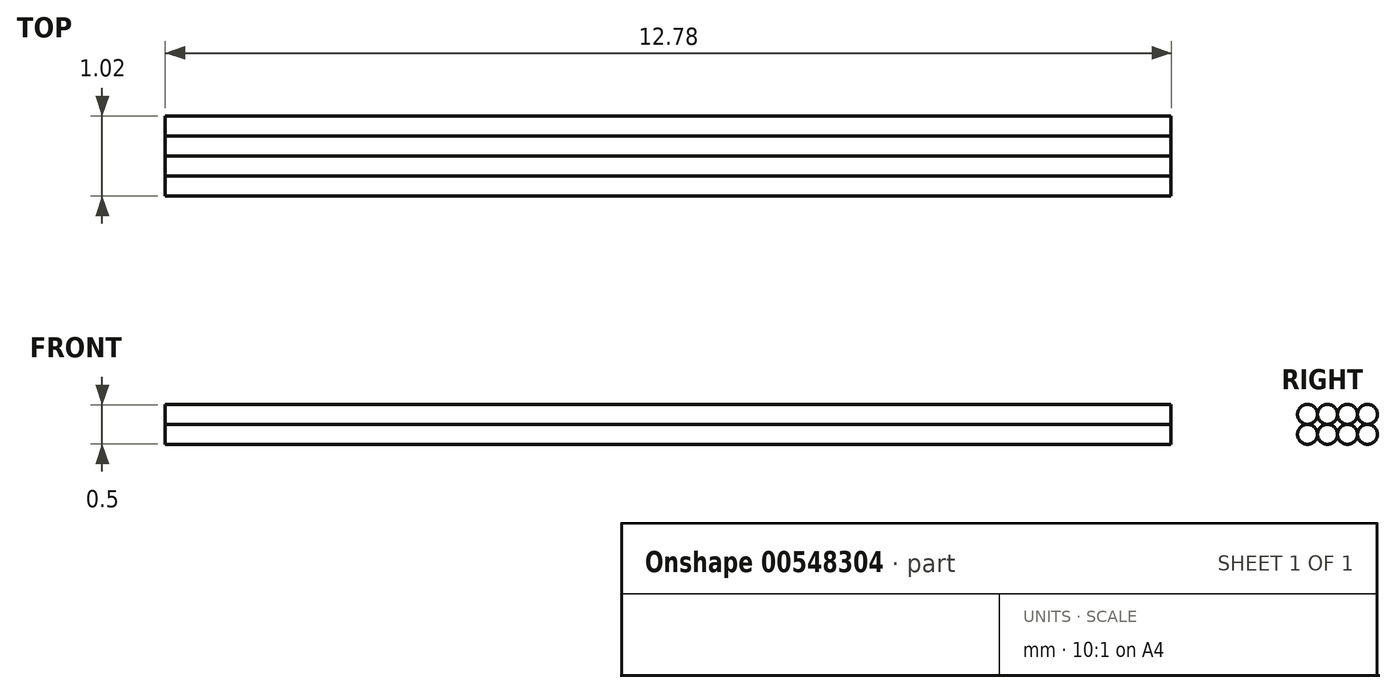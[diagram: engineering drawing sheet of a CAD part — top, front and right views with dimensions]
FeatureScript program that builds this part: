
annotation { "Feature Type Name" : "Feature", "Feature Type Description" : "" }
export const myFeature = defineFeature(function(context is Context, id is Id, definition is map)
    precondition{}
    {
        {
            var Q0;
            Q0=qCreatedBy(makeId("Right.planeOp"),FACE);
            var sketch = newSketch(context, id + "F0", { "sketchPlane" : qUnion([Q0])});
            skLineSegment(sketch, "E0.bottom", {"start": v(0.5, -0.25) * mm, "end": v(-0.5, -0.25) * mm, "construction": true});
            skLineSegment(sketch, "E0.top", {"start": v(0.5, 0.25) * mm, "end": v(-0.5, 0.25) * mm, "construction": true});
            skLineSegment(sketch, "E0.left", {"start": v(0.5, -0.25) * mm, "end": v(0.5, 0.25) * mm, "construction": true});
            skLineSegment(sketch, "E0.right", {"start": v(-0.5, -0.25) * mm, "end": v(-0.5, 0.25) * mm, "construction": true});
            skPoint(sketch, "E0.middle", {"position": v(0, 0) * mm});
            skCircle(sketch, "E1", {"center": v(-0.38, 0.13) * mm, "radius": 0.13 * mm});
            skCircle(sketch, "E2.1.0.0", {"center": v(-0.13, 0.13) * mm, "radius": 0.13 * mm});
            skCircle(sketch, "E2.2.0.0", {"center": v(0.13, 0.13) * mm, "radius": 0.13 * mm});
            skCircle(sketch, "E2.3.0.0", {"center": v(0.38, 0.13) * mm, "radius": 0.13 * mm});
            skLineSegment(sketch, "E2.direction1", {"start": v(-0.38, 0.13) * mm, "end": v(-0.13, 0.13) * mm, "construction": true});
            skCircle(sketch, "E3", {"center": v(-0.38, -0.13) * mm, "radius": 0.13 * mm});
            skCircle(sketch, "E4.1.0.0", {"center": v(-0.13, -0.13) * mm, "radius": 0.13 * mm});
            skCircle(sketch, "E4.2.0.0", {"center": v(0.13, -0.13) * mm, "radius": 0.13 * mm});
            skCircle(sketch, "E4.3.0.0", {"center": v(0.38, -0.13) * mm, "radius": 0.13 * mm});
            skLineSegment(sketch, "E4.direction1", {"start": v(-0.38, -0.13) * mm, "end": v(-0.13, -0.13) * mm, "construction": true});
            skSolve(sketch);
        }
        {
            var Q0;
            {var subQ0=sQuery(id+"F0.wireOp",EDGE,"E1");var subQ1=makeQuery(id+"F0.imprint","INTERSECT",VERTEX,{"derivedFrom":[subQ0,sQuery(id+"F0.wireOp",EDGE,"E2.1.0.0")]});Q0=makeQuery(id+"F0.imprint","IMPRINT",FACE,{"disambiguationData":[TD([[makeQuery(id+"F0.imprint","IMPRINT",EDGE,{"disambiguationData":[TD([[subQ1,-1.0]])],"derivedFrom":subQ0}),1.0]])]});}
            var Q1;
            {var subQ0=sQuery(id+"F0.wireOp",EDGE,"E2.1.0.0");var subQ1=makeQuery(id+"F0.imprint","INTERSECT",VERTEX,{"derivedFrom":[sQuery(id+"F0.wireOp",EDGE,"E1"),subQ0]});Q1=makeQuery(id+"F0.imprint","IMPRINT",FACE,{"disambiguationData":[TD([[makeQuery(id+"F0.imprint","IMPRINT",EDGE,{"disambiguationData":[TD([[subQ1,1.0]])],"derivedFrom":subQ0}),1.0]])]});}
            var Q2;
            {var subQ0=sQuery(id+"F0.wireOp",EDGE,"E4.1.0.0");var subQ1=makeQuery(id+"F0.imprint","INTERSECT",VERTEX,{"derivedFrom":[subQ0,sQuery(id+"F0.wireOp",EDGE,"E4.2.0.0")]});Q2=makeQuery(id+"F0.imprint","IMPRINT",FACE,{"disambiguationData":[TD([[makeQuery(id+"F0.imprint","IMPRINT",EDGE,{"disambiguationData":[TD([[subQ1,-1.0]])],"derivedFrom":subQ0}),1.0]])]});}
            var Q3;
            {var subQ0=sQuery(id+"F0.wireOp",EDGE,"E2.2.0.0");var subQ1=makeQuery(id+"F0.imprint","INTERSECT",VERTEX,{"derivedFrom":[sQuery(id+"F0.wireOp",EDGE,"E2.1.0.0"),subQ0]});Q3=makeQuery(id+"F0.imprint","IMPRINT",FACE,{"disambiguationData":[TD([[makeQuery(id+"F0.imprint","IMPRINT",EDGE,{"disambiguationData":[TD([[subQ1,1.0]])],"derivedFrom":subQ0}),1.0]])]});}
            var Q4;
            {var subQ0=sQuery(id+"F0.wireOp",EDGE,"E3");var subQ1=makeQuery(id+"F0.imprint","INTERSECT",VERTEX,{"derivedFrom":[sQuery(id+"F0.wireOp",EDGE,"E1"),subQ0]});Q4=makeQuery(id+"F0.imprint","IMPRINT",FACE,{"disambiguationData":[TD([[makeQuery(id+"F0.imprint","IMPRINT",EDGE,{"disambiguationData":[TD([[subQ1,1.0]])],"derivedFrom":subQ0}),1.0]])]});}
            var Q5;
            {var subQ0=sQuery(id+"F0.wireOp",EDGE,"E4.2.0.0");var subQ1=makeQuery(id+"F0.imprint","INTERSECT",VERTEX,{"derivedFrom":[subQ0,sQuery(id+"F0.wireOp",EDGE,"E4.3.0.0")]});Q5=makeQuery(id+"F0.imprint","IMPRINT",FACE,{"disambiguationData":[TD([[makeQuery(id+"F0.imprint","IMPRINT",EDGE,{"disambiguationData":[TD([[subQ1,-1.0]])],"derivedFrom":subQ0}),1.0]])]});}
            var Q6;
            {var subQ0=sQuery(id+"F0.wireOp",EDGE,"E2.3.0.0");var subQ1=makeQuery(id+"F0.imprint","INTERSECT",VERTEX,{"derivedFrom":[sQuery(id+"F0.wireOp",EDGE,"E2.2.0.0"),subQ0]});Q6=makeQuery(id+"F0.imprint","IMPRINT",FACE,{"disambiguationData":[TD([[makeQuery(id+"F0.imprint","IMPRINT",EDGE,{"disambiguationData":[TD([[subQ1,-1.0]])],"derivedFrom":subQ0}),1.0]])]});}
            var Q7;
            {var subQ0=sQuery(id+"F0.wireOp",EDGE,"E4.3.0.0");var subQ1=makeQuery(id+"F0.imprint","INTERSECT",VERTEX,{"derivedFrom":[sQuery(id+"F0.wireOp",EDGE,"E2.3.0.0"),subQ0]});Q7=makeQuery(id+"F0.imprint","IMPRINT",FACE,{"disambiguationData":[TD([[makeQuery(id+"F0.imprint","IMPRINT",EDGE,{"disambiguationData":[TD([[subQ1,-1.0]])],"derivedFrom":subQ0}),1.0]])]});}
            var Q8;
            Q8=sQuery(id+"F0.wireOp",EDGE,"E0.top");
            var Q9;
            Q9=sQuery(id+"F0.wireOp",EDGE,"E0.right");
            var Q10;
            Q10=sQuery(id+"F0.wireOp",EDGE,"E0.bottom");
            var Q11;
            Q11=sQuery(id+"F0.wireOp",EDGE,"E0.left");
            var Q12;
            Q12=sQuery(id+"F0.wireOp",EDGE,"E1");
            var Q13;
            Q13=sQuery(id+"F0.wireOp",EDGE,"E2.1.0.0");
            var Q14;
            Q14=sQuery(id+"F0.wireOp",EDGE,"E2.2.0.0");
            var Q15;
            Q15=sQuery(id+"F0.wireOp",EDGE,"E2.3.0.0");
            var Q16;
            Q16=sQuery(id+"F0.wireOp",EDGE,"E4.3.0.0");
            var Q17;
            Q17=sQuery(id+"F0.wireOp",EDGE,"E4.2.0.0");
            var Q18;
            Q18=sQuery(id+"F0.wireOp",EDGE,"E4.1.0.0");
            var Q19;
            Q19=sQuery(id+"F0.wireOp",EDGE,"E3");
            extrude(context, id + "F1", {"entities" : qUnion([Q0, Q1, Q2, Q3, Q4, Q5, Q6, Q7]), "surfaceEntities" : qUnion([Q8, Q9, Q10, Q11, Q12, Q13, Q14, Q15, Q16, Q17, Q18, Q19]), "depth" : 12.78 * mm, "offsetDistance" : 25.4 * mm});
        }
    });
